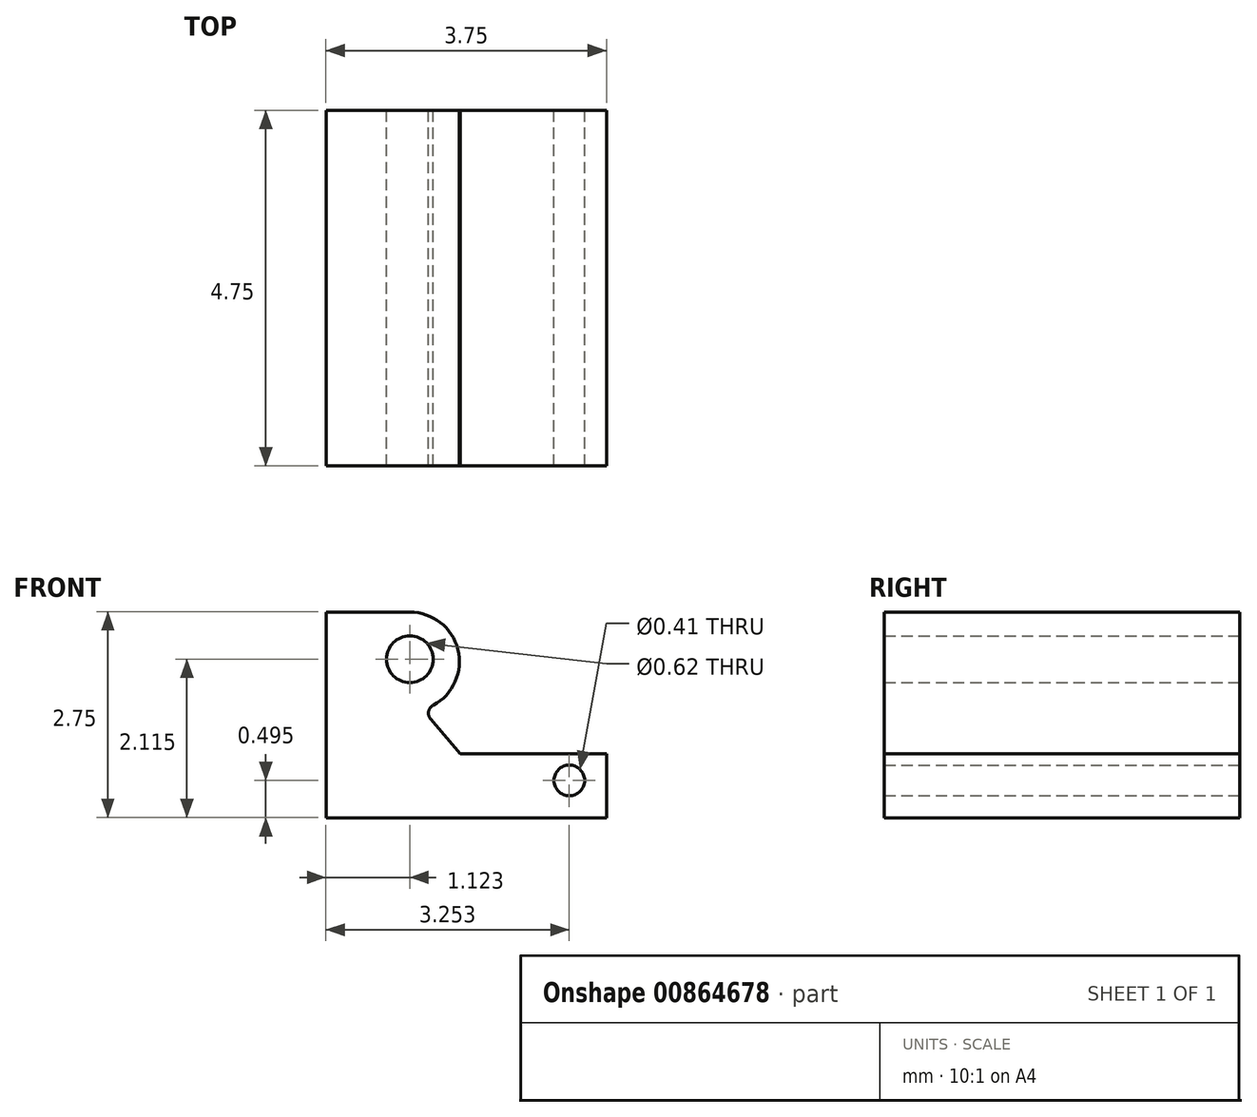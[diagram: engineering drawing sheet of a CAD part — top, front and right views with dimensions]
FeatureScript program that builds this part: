
annotation { "Feature Type Name" : "Feature", "Feature Type Description" : "" }
export const myFeature = defineFeature(function(context is Context, id is Id, definition is map)
    precondition{}
    {
        {
            var Q0;
            Q0=qCreatedBy(makeId("Front.planeOp"),FACE);
            var sketch = newSketch(context, id + "F0", { "sketchPlane" : qUnion([Q0])});
            skLineSegment(sketch, "E0", {"start": v(-7.06, 5.84) * mm, "end": v(-5.94, 5.84) * mm});
            skLineSegment(sketch, "E1", {"start": v(-3.3, 3.94) * mm, "end": v(-3.3, 3.09) * mm});
            skLineSegment(sketch, "E2", {"start": v(-3.3, 3.09) * mm, "end": v(-7.06, 3.09) * mm});
            skLineSegment(sketch, "E3", {"start": v(-7.06, 3.09) * mm, "end": v(-7.06, 5.84) * mm});
            skLineSegment(sketch, "E4", {"start": v(-5.94, 5.84) * mm, "end": v(-5.94, 5.52) * mm});
            skLineSegment(sketch, "E5", {"start": v(-7.06, 3.09) * mm, "end": v(-3.8, 3.09) * mm});
            skLineSegment(sketch, "E6", {"start": v(-7.06, 3.09) * mm, "end": v(-6.8, 3.09) * mm});
            skLineSegment(sketch, "E7", {"start": v(-6.8, 3.09) * mm, "end": v(-6.8, 5.84) * mm});
            skPoint(sketch, "E7.endSnap0", {"position": v(-6.5, 5.84) * mm});
            skLineSegment(sketch, "E8", {"start": v(-6.8, 5.84) * mm, "end": v(-7.06, 5.84) * mm});
            skLineSegment(sketch, "E9", {"start": v(-3.3, 3.94) * mm, "end": v(-3.3, 3.59) * mm});
            skLineSegment(sketch, "E10", {"start": v(-3.3, 3.09) * mm, "end": v(-4.3, 3.09) * mm});
            skLineSegment(sketch, "E11", {"start": v(-3.3, 3.59) * mm, "end": v(-3.8, 3.59) * mm});
            skLineSegment(sketch, "E12", {"start": v(-3.8, 3.59) * mm, "end": v(-3.8, 3.09) * mm});
            skCircle(sketch, "E13", {"center": v(-3.8, 3.59) * mm, "radius": 0.2 * mm});
            skLineSegment(sketch, "E14", {"start": v(-3.3, 3.59) * mm, "end": v(-3.3, 3.94) * mm});
            skCircle(sketch, "E15", {"center": v(-5.94, 5.2) * mm, "radius": 0.31 * mm});
            skArc(sketch, "E16", {"start": v(-5.94, 5.84) * mm, "mid": v(-5.3, 5.33) * mm, "end": v(-5.63, 4.6) * mm});
            skLineSegment(sketch, "E17", {"start": v(-3.3, -3.68) * mm, "end": v(-5.94, -3.68) * mm});
            skPoint(sketch, "E18.visualSharp", {"position": v(-5.94, 4.51) * mm});
            skLineSegment(sketch, "E19", {"start": v(-3.3, 3.94) * mm, "end": v(-5.26, 3.94) * mm});
            skLineSegment(sketch, "E20", {"start": v(-5.26, 3.94) * mm, "end": v(-5.66, 4.4) * mm});
            skPoint(sketch, "E21.visualSharp", {"position": v(-5.77, 4.53) * mm});
            skArc(sketch, "E21.filletArc", {"start": v(-5.63, 4.6) * mm, "mid": v(-5.69, 4.5) * mm, "end": v(-5.66, 4.4) * mm});
            skSolve(sketch);
        }
        {
            var Q0;
            Q0 = qSketchRegion(id + "F0", true);
            extrude(context, id + "F1", {"entities" : qUnion([Q0]), "depth" : 4.75 * mm, "offsetDistance" : 25 * mm});
        }
    });
